# Revit family: Mounting Brackets PNR-05500
name_source: partatom
category: Generic Models
revit_build: Autodesk Revit 2017 (Build: 20190508_0315(x64)
units: mm (PartAtom-declared; Revit-internal decimal feet)

## family parameters
Always vertical = No
Can host rebar = No
Cut with Voids When Loaded = No
Part Type = Normal
Room Calculation Point = No
Round Connector Dimension = Use Diameter
Shared = No
Work Plane-Based = Yes

## types (11) — shared parameters
Bolt_Material = Brass, Soft Yellow, Welded
Bracket Article Number = *User Defined
Default Elevation = 1219 mm
Define - Bracket Article Number = https://www.veko.com
Description = Mounting Brackets
Manufacturer = Veko Lightsystems
Mounting_Material = Aluminum 7175 T73 0 Hot Formed
Pendulum Visiblity = No

## per-type parameters (varying)
| type | 61-B1-R | 61-B3-CR | 61-B3-R | Assembly Code | B1-R | B3-CR | B3-R | B7-R | B7SO-R | BT30-R | BT45-R | BT60-R | Bolt_Visibility | Bracket_Width | Pendulum Start |
| B1-R | No | No | No | 63.0 | Yes | No | No | No | No | No | No | No | No | 15 mm  [stored 0.0492126 ft] | 35 mm |
| B3-R | No | No | No | 63.0 | No | No | Yes | No | No | No | No | No | Yes | 15 mm  [stored 0.0492126 ft] | 23 mm |
| B3-CR | No | No | No | 63.0 | No | Yes | No | No | No | No | No | No | Yes | 15 mm  [stored 0.0492126 ft] | 24 mm |
| 61-B1-R | Yes | No | No | 63.0 | No | No | No | No | No | No | No | No | No | 15 mm  [stored 0.0492126 ft] | 31 mm  [stored 0.101706 ft] |
| 61-B3-R | No | No | Yes | 63.0 | No | No | No | No | No | No | No | No | No | 15 mm  [stored 0.0492126 ft] | 29 mm |
| 61-B3-CR | No | Yes | No | 63.0 | No | No | No | No | No | No | No | No | No | 15 mm  [stored 0.0492126 ft] | 31 mm  [stored 0.101706 ft] |
| B7SO-R | No | No | No | 63.0 | No | No | No | No | Yes | No | No | No | Yes | 15 mm  [stored 0.0492126 ft] | 34 mm |
| B7-R | No | No | No | 63.0 | No | No | No | Yes | No | No | No | No | Yes | 15 mm  [stored 0.0492126 ft] | 88 mm |
| BT30-R | No | No | No | 63.0 | No | No | No | No | No | Yes | No | No | No | 18 mm  [stored 0.0590551 ft] | 23 mm |
| BT45-R | No | No | No | 63.0 | No | No | No | No | No | No | Yes | No | No | 15 mm  [stored 0.0492126 ft] | 23 mm |
| BT60-R | No | No | No |  | No | No | No | No | No | No | No | Yes | No | 15 mm  [stored 0.0492126 ft] | 23 mm |

note: column(s) folded — value = type name in every type: Model

note: [stored X ft] marks values corroborated as IEEE doubles in the binary element streams (Revit-internal decimal feet)

## geometry (parser evidence)
native form markers: Sweep x3
no freeform markers — native parametric forms only
